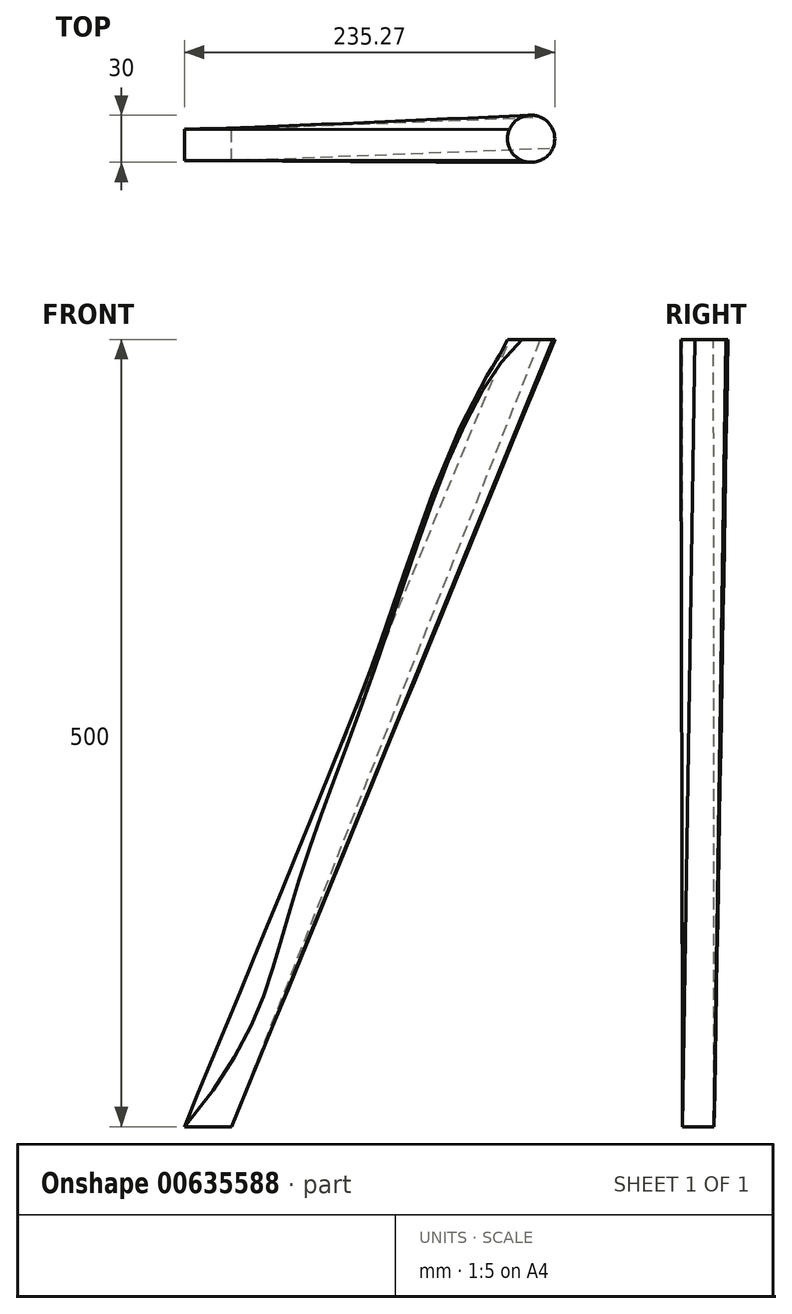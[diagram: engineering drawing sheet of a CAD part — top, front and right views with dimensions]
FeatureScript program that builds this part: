
annotation { "Feature Type Name" : "Feature", "Feature Type Description" : "" }
export const myFeature = defineFeature(function(context is Context, id is Id, definition is map)
    precondition{}
    {
        {
            var Q0;
            Q0=qCreatedBy(makeId("Top.planeOp"),FACE);
            var sketch = newSketch(context, id + "F0", { "sketchPlane" : qUnion([Q0])});
            skLineSegment(sketch, "E0.bottom", {"start": v(0, 0) * mm, "end": v(30, 0) * mm});
            skLineSegment(sketch, "E0.top", {"start": v(0, 20) * mm, "end": v(30, 20) * mm});
            skLineSegment(sketch, "E0.left", {"start": v(0, 0) * mm, "end": v(0, 20) * mm});
            skLineSegment(sketch, "E0.right", {"start": v(30, 0) * mm, "end": v(30, 20) * mm});
            skSolve(sketch);
        }
        {
            var Q0;
            Q0=qCreatedBy(makeId("Top.planeOp"),FACE);
            cPlane(context, id + "F1", {"entities" : qUnion([Q0]), "cplaneType" : CPlaneType.OFFSET, "offset" : 500 * mm, "width" : 150 * mm, "height" : 150 * mm});
        }
        {
            var Q0;
            Q0=qCreatedBy(makeId("Front.planeOp"),FACE);
            var sketch = newSketch(context, id + "F2", { "sketchPlane" : qUnion([Q0])});
            skFitSpline(sketch, "E1", {"points": [v(0, 0) * mm, v(67.5, 139.58) * mm, v(127.6, 310.1) * mm, v(214.39, 500) * mm], "startDerivative": vector(470.35, 554.45) * mm, "endDerivative": vector(311.2, 279.47) * mm});
            skSolve(sketch);
        }
        {
            var Q0;
            Q0=qCreatedBy(id+"F1.planeOp",FACE);
            var sketch = newSketch(context, id + "F3", { "sketchPlane" : qUnion([Q0])});
            skCircle(sketch, "E2", {"center": v(220.27, 13.8) * mm, "radius": 15 * mm});
            skSolve(sketch);
        }
        {
            var Q0;
            Q0=makeQuery(id+"F0.imprint","IMPRINT",FACE,{"disambiguationData":[TD([[makeQuery(id+"F0.imprint","IMPRINT",EDGE,{"derivedFrom":sQuery(id+"F0.wireOp",EDGE,"E0.bottom")}),1.0]])]});
            var Q1;
            Q1=makeQuery(id+"F3.imprint","IMPRINT",FACE,{"disambiguationData":[TD([[makeQuery(id+"F3.imprint","IMPRINT",EDGE,{"derivedFrom":sQuery(id+"F3.wireOp",EDGE,"E2")}),1.0]])]});
            var Q2;
            Q2=sQuery(id+"F2.wireOp",EDGE,"E1");
            loft(context, id + "F4", {"addGuides" : true, "sheetProfilesArray" : [{ "sheetProfileEntities" : qUnion([Q0]) }, { "sheetProfileEntities" : qUnion([Q1]) }], "guidesArray" : [{ "guideEntities" : qUnion([Q2]), "guideDerivativeType" : LoftGuideDerivativeType.DEFAULT, "guideDerivativeMagnitude" : 1 }]});
        }
    });
